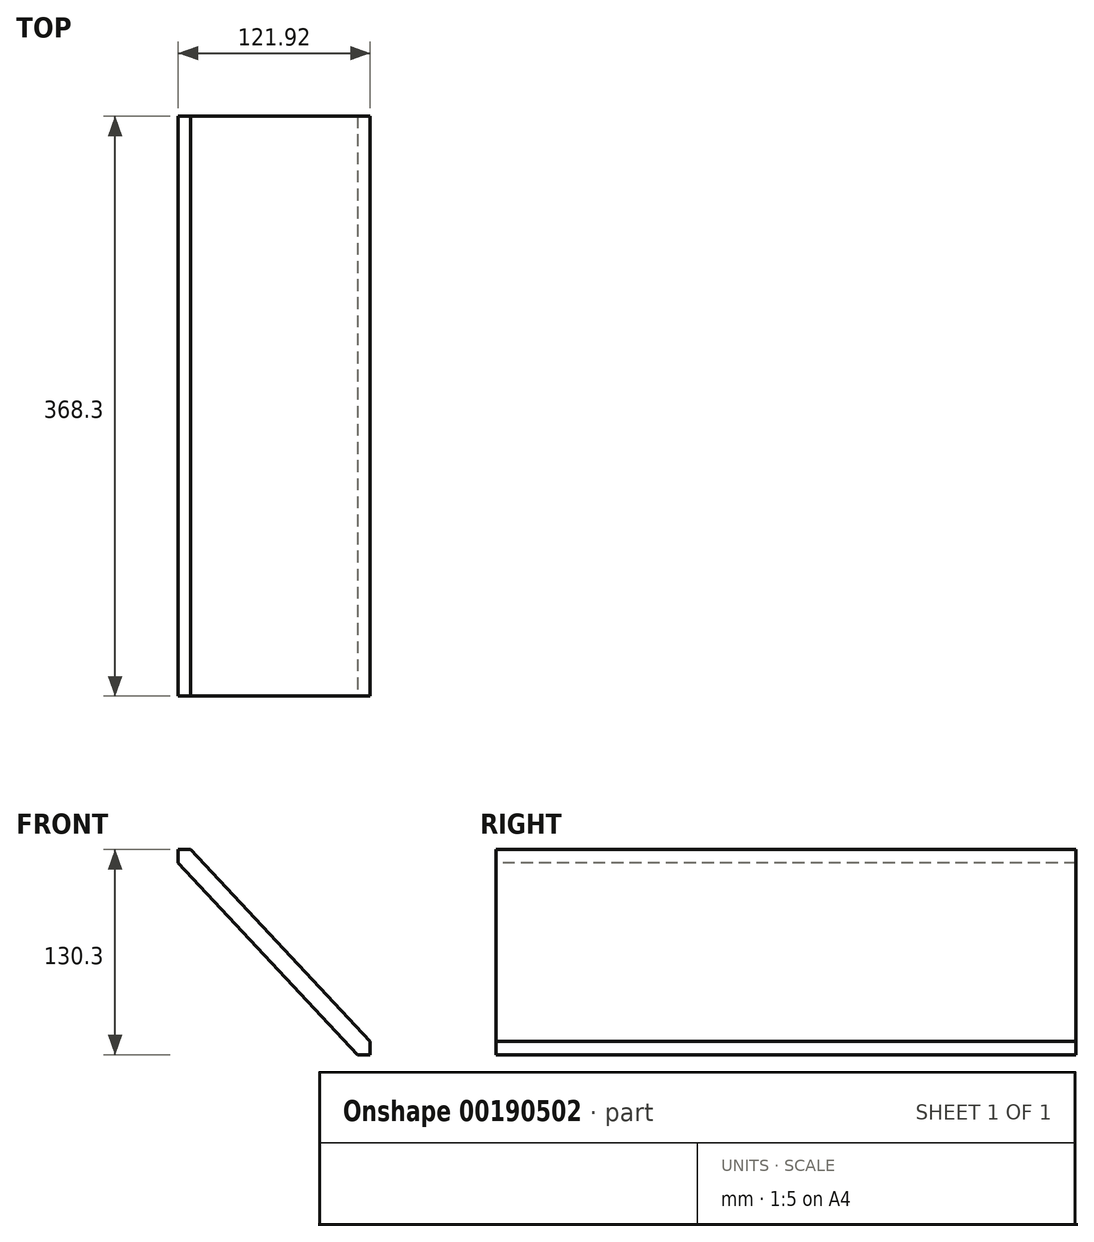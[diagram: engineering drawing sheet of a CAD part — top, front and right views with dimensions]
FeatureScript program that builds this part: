
annotation { "Feature Type Name" : "Feature", "Feature Type Description" : "" }
export const myFeature = defineFeature(function(context is Context, id is Id, definition is map)
    precondition{}
    {
        {
            var Q0;
            Q0=qCreatedBy(makeId("Front.planeOp"),FACE);
            var sketch = newSketch(context, id + "F0", { "sketchPlane" : qUnion([Q0])});
            skLineSegment(sketch, "E0.bottom", {"start": v(0, 0) * mm, "end": v(7.88, 0) * mm});
            skLineSegment(sketch, "E0.top", {"start": v(114.04, -130.3) * mm, "end": v(121.92, -130.3) * mm});
            skLineSegment(sketch, "E0.left", {"start": v(0, 0) * mm, "end": v(0, -8.42) * mm});
            skLineSegment(sketch, "E0.right", {"start": v(121.92, -121.88) * mm, "end": v(121.92, -130.3) * mm});
            skLineSegment(sketch, "E1", {"start": v(0, 0) * mm, "end": v(121.92, -130.3) * mm, "construction": true});
            skLineSegment(sketch, "E2", {"start": v(114.04, -130.3) * mm, "end": v(0, -8.42) * mm});
            skLineSegment(sketch, "E3.MirrorCS", {"start": v(121.92, -121.88) * mm, "end": v(7.88, 0) * mm});
            skPoint(sketch, "E4.orphan", {"position": v(-1.63, 10.16) * mm});
            skPoint(sketch, "E5.orphan", {"position": v(-10.03, 2.3) * mm});
            skPoint(sketch, "E6.orphan", {"position": v(122.44, -122.44) * mm});
            skSolve(sketch);
        }
        {
            var Q0;
            Q0=makeQuery(id+"F0.imprint","IMPRINT",FACE,{"disambiguationData":[TD([[makeQuery(id+"F0.imprint","IMPRINT",EDGE,{"derivedFrom":sQuery(id+"F0.wireOp",EDGE,"E0.bottom")}),-1.0]])]});
            var Q1;
            Q1 = qConstructionFilter(qBodyType(qCreatedBy(id + "F0" ,EDGE), BodyType.WIRE), ConstructionObject.NO);
            extrude(context, id + "F1", {"entities" : qUnion([Q0]), "surfaceEntities" : qUnion([Q1]), "oppositeDirection" : true, "depth" : 368.3 * mm});
        }
    });
